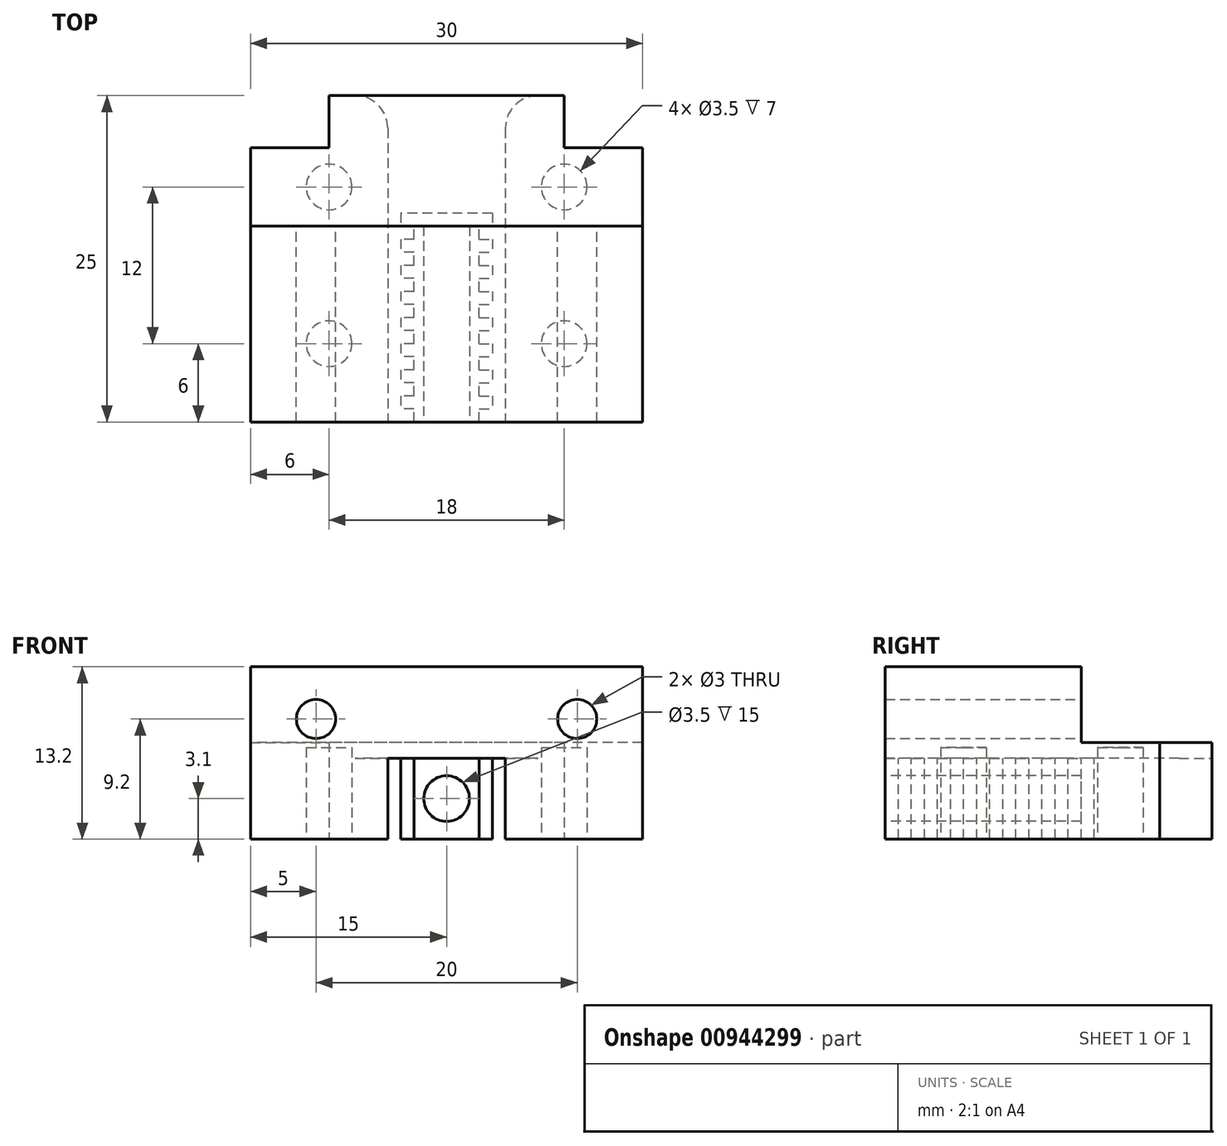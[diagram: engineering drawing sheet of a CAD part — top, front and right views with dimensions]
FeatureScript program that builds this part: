
annotation { "Feature Type Name" : "Feature", "Feature Type Description" : "" }
export const myFeature = defineFeature(function(context is Context, id is Id, definition is map)
    precondition{}
    {
        {
            var Q0;
            Q0=qCreatedBy(makeId("Front.planeOp"),FACE);
            var sketch = newSketch(context, id + "F0", { "sketchPlane" : qUnion([Q0])});
            skLineSegment(sketch, "E0.bottom", {"start": v(15, -3) * mm, "end": v(-15, -3) * mm});
            skLineSegment(sketch, "E0.top", {"start": v(15, 4) * mm, "end": v(-15, 4) * mm});
            skLineSegment(sketch, "E0.left", {"start": v(15, -3) * mm, "end": v(15, 4) * mm});
            skLineSegment(sketch, "E0.right", {"start": v(-15, -3) * mm, "end": v(-15, 4) * mm});
            skPoint(sketch, "E0.middle", {"position": v(0, 0) * mm});
            skCircle(sketch, "E1", {"center": v(-10, 0) * mm, "radius": 1.5 * mm});
            skCircle(sketch, "E2.MirrorC", {"center": v(10, 0) * mm, "radius": 1.5 * mm});
            skSolve(sketch);
        }
        {
            var Q0;
            Q0=makeQuery(id+"F0.imprint","IMPRINT",FACE,{"disambiguationData":[TD([[makeQuery(id+"F0.imprint","IMPRINT",EDGE,{"derivedFrom":sQuery(id+"F0.wireOp",EDGE,"E0.bottom")}),-1.0]])]});
            extrude(context, id + "F1", {"entities" : qUnion([Q0]), "depth" : 25 * mm, "offsetDistance" : 25 * mm});
        }
        {
            var Q0;
            Q0=makeQuery(id+"F1.opExtrude","SWEPT_FACE",FACE,{"disambiguationData":[OSD([sQuery(id+"F0.wireOp",EDGE,"E0.bottom")])]});
            var sketch = newSketch(context, id + "F2", { "sketchPlane" : qUnion([Q0])});
            skLineSegment(sketch, "E3", {"start": v(-2.5, 25) * mm, "end": v(-2.5, 24) * mm});
            skLineSegment(sketch, "E4.top", {"start": v(-3.5, 23) * mm, "end": v(-3.5, 24) * mm});
            skLineSegment(sketch, "E4.left", {"start": v(-2.5, 23) * mm, "end": v(-3.5, 23) * mm});
            skLineSegment(sketch, "E4.right", {"start": v(-2.5, 24) * mm, "end": v(-3.5, 24) * mm});
            skLineSegment(sketch, "E5.1.0.0", {"start": v(-2.5, 21) * mm, "end": v(-3.5, 21) * mm});
            skLineSegment(sketch, "E5.1.0.1", {"start": v(-3.5, 21) * mm, "end": v(-3.5, 22) * mm});
            skLineSegment(sketch, "E5.1.0.2", {"start": v(-2.5, 23) * mm, "end": v(-2.5, 22) * mm});
            skLineSegment(sketch, "E5.1.0.3", {"start": v(-2.5, 22) * mm, "end": v(-3.5, 22) * mm});
            skLineSegment(sketch, "E5.2.0.0", {"start": v(-2.5, 19) * mm, "end": v(-3.5, 19) * mm});
            skLineSegment(sketch, "E5.2.0.1", {"start": v(-3.5, 19) * mm, "end": v(-3.5, 20) * mm});
            skLineSegment(sketch, "E5.2.0.2", {"start": v(-2.5, 21) * mm, "end": v(-2.5, 20) * mm});
            skLineSegment(sketch, "E5.2.0.3", {"start": v(-2.5, 20) * mm, "end": v(-3.5, 20) * mm});
            skLineSegment(sketch, "E5.3.0.0", {"start": v(-2.5, 17) * mm, "end": v(-3.5, 17) * mm});
            skLineSegment(sketch, "E5.3.0.1", {"start": v(-3.5, 17) * mm, "end": v(-3.5, 18) * mm});
            skLineSegment(sketch, "E5.3.0.2", {"start": v(-2.5, 19) * mm, "end": v(-2.5, 18) * mm});
            skLineSegment(sketch, "E5.3.0.3", {"start": v(-2.5, 18) * mm, "end": v(-3.5, 18) * mm});
            skLineSegment(sketch, "E5.4.0.0", {"start": v(-2.5, 15) * mm, "end": v(-3.5, 15) * mm});
            skLineSegment(sketch, "E5.4.0.1", {"start": v(-3.5, 15) * mm, "end": v(-3.5, 16) * mm});
            skLineSegment(sketch, "E5.4.0.2", {"start": v(-2.5, 17) * mm, "end": v(-2.5, 16) * mm});
            skLineSegment(sketch, "E5.4.0.3", {"start": v(-2.5, 16) * mm, "end": v(-3.5, 16) * mm});
            skLineSegment(sketch, "E5.5.0.0", {"start": v(-2.5, 13) * mm, "end": v(-3.5, 13) * mm});
            skLineSegment(sketch, "E5.5.0.1", {"start": v(-3.5, 13) * mm, "end": v(-3.5, 14) * mm});
            skLineSegment(sketch, "E5.5.0.2", {"start": v(-2.5, 15) * mm, "end": v(-2.5, 14) * mm});
            skLineSegment(sketch, "E5.5.0.3", {"start": v(-2.5, 14) * mm, "end": v(-3.5, 14) * mm});
            skLineSegment(sketch, "E5.6.0.0", {"start": v(-2.5, 11) * mm, "end": v(-3.5, 11) * mm});
            skLineSegment(sketch, "E5.6.0.1", {"start": v(-3.5, 11) * mm, "end": v(-3.5, 12) * mm});
            skLineSegment(sketch, "E5.6.0.2", {"start": v(-2.5, 13) * mm, "end": v(-2.5, 12) * mm});
            skLineSegment(sketch, "E5.6.0.3", {"start": v(-2.5, 12) * mm, "end": v(-3.5, 12) * mm});
            skLineSegment(sketch, "E5.7.0.0", {"start": v(-2.5, 9) * mm, "end": v(-3.5, 9) * mm});
            skLineSegment(sketch, "E5.7.0.1", {"start": v(-3.5, 9) * mm, "end": v(-3.5, 10) * mm});
            skLineSegment(sketch, "E5.7.0.2", {"start": v(-2.5, 11) * mm, "end": v(-2.5, 10) * mm});
            skLineSegment(sketch, "E5.7.0.3", {"start": v(-2.5, 10) * mm, "end": v(-3.5, 10) * mm});
            skLineSegment(sketch, "E5.direction1", {"start": v(-2.5, 23) * mm, "end": v(-2.5, 21) * mm, "construction": true});
            skLineSegment(sketch, "E6", {"start": v(0, 0) * mm, "end": v(0, 25) * mm, "construction": true});
            skLineSegment(sketch, "E7.MirrorCS", {"start": v(2.5, 23) * mm, "end": v(2.5, 22) * mm});
            skLineSegment(sketch, "E8.MirrorCS", {"start": v(2.5, 25) * mm, "end": v(2.5, 24) * mm});
            skLineSegment(sketch, "E9.MirrorCS", {"start": v(2.5, 19) * mm, "end": v(3.5, 19) * mm});
            skLineSegment(sketch, "E10.MirrorCS", {"start": v(2.5, 16) * mm, "end": v(3.5, 16) * mm});
            skLineSegment(sketch, "E11.MirrorCS", {"start": v(2.5, 18) * mm, "end": v(3.5, 18) * mm});
            skLineSegment(sketch, "E12.MirrorCS", {"start": v(2.5, 22) * mm, "end": v(3.5, 22) * mm});
            skLineSegment(sketch, "E13.MirrorCS", {"start": v(2.5, 21) * mm, "end": v(3.5, 21) * mm});
            skLineSegment(sketch, "E14.MirrorCS", {"start": v(3.5, 9) * mm, "end": v(3.5, 10) * mm});
            skLineSegment(sketch, "E15.MirrorCS", {"start": v(2.5, 24) * mm, "end": v(3.5, 24) * mm});
            skLineSegment(sketch, "E16.MirrorCS", {"start": v(2.5, 9) * mm, "end": v(3.5, 9) * mm});
            skLineSegment(sketch, "E17.MirrorCS", {"start": v(2.5, 21) * mm, "end": v(2.5, 20) * mm});
            skLineSegment(sketch, "E18.MirrorCS", {"start": v(3.5, 11) * mm, "end": v(3.5, 12) * mm});
            skLineSegment(sketch, "E19.MirrorCS", {"start": v(2.5, 12) * mm, "end": v(3.5, 12) * mm});
            skLineSegment(sketch, "E20.MirrorCS", {"start": v(2.5, 17) * mm, "end": v(2.5, 16) * mm});
            skLineSegment(sketch, "E21.MirrorCS", {"start": v(2.5, 23) * mm, "end": v(2.5, 21) * mm, "construction": true});
            skLineSegment(sketch, "E22.MirrorCS", {"start": v(2.5, 15) * mm, "end": v(3.5, 15) * mm});
            skLineSegment(sketch, "E23.MirrorCS", {"start": v(3.5, 19) * mm, "end": v(3.5, 20) * mm});
            skLineSegment(sketch, "E24.MirrorCS", {"start": v(3.5, 15) * mm, "end": v(3.5, 16) * mm});
            skLineSegment(sketch, "E25.MirrorCS", {"start": v(2.5, 19) * mm, "end": v(2.5, 18) * mm});
            skLineSegment(sketch, "E26.MirrorCS", {"start": v(3.5, 21) * mm, "end": v(3.5, 22) * mm});
            skLineSegment(sketch, "E27.MirrorCS", {"start": v(2.5, 15) * mm, "end": v(2.5, 14) * mm});
            skLineSegment(sketch, "E28.MirrorCS", {"start": v(3.5, 23) * mm, "end": v(3.5, 24) * mm});
            skLineSegment(sketch, "E29.MirrorCS", {"start": v(2.5, 13) * mm, "end": v(2.5, 12) * mm});
            skLineSegment(sketch, "E30.MirrorCS", {"start": v(2.5, 20) * mm, "end": v(3.5, 20) * mm});
            skLineSegment(sketch, "E31.MirrorCS", {"start": v(2.5, 11) * mm, "end": v(2.5, 10) * mm});
            skLineSegment(sketch, "E32.MirrorCS", {"start": v(2.5, 14) * mm, "end": v(3.5, 14) * mm});
            skLineSegment(sketch, "E33.MirrorCS", {"start": v(3.5, 13) * mm, "end": v(3.5, 14) * mm});
            skLineSegment(sketch, "E34.MirrorCS", {"start": v(2.5, 23) * mm, "end": v(3.5, 23) * mm});
            skLineSegment(sketch, "E35.MirrorCS", {"start": v(2.5, 17) * mm, "end": v(3.5, 17) * mm});
            skLineSegment(sketch, "E36.MirrorCS", {"start": v(2.5, 13) * mm, "end": v(3.5, 13) * mm});
            skLineSegment(sketch, "E37.MirrorCS", {"start": v(3.5, 17) * mm, "end": v(3.5, 18) * mm});
            skLineSegment(sketch, "E38.MirrorCS", {"start": v(2.5, 11) * mm, "end": v(3.5, 11) * mm});
            skLineSegment(sketch, "E39.MirrorCS", {"start": v(2.5, 10) * mm, "end": v(3.5, 10) * mm});
            skLineSegment(sketch, "E40.MirrorCS", {"start": v(4.5, 2.5) * mm, "end": v(4.5, 25) * mm});
            skLineSegment(sketch, "E41", {"start": v(15, 25) * mm, "end": v(4.5, 25) * mm});
            skLineSegment(sketch, "E42", {"start": v(2.5, 9) * mm, "end": v(-2.5, 9) * mm});
            skArc(sketch, "E43", {"start": v(4.5, 2.5) * mm, "mid": v(5.23, 0.73) * mm, "end": v(7, 0) * mm});
            skPoint(sketch, "E43.third.point", {"position": v(4.69, 1.55) * mm});
            skLineSegment(sketch, "E44.MirrorCS", {"start": v(-15, 25) * mm, "end": v(-4.5, 25) * mm});
            skLineSegment(sketch, "E45.MirrorCS", {"start": v(-4.5, 2.5) * mm, "end": v(-4.5, 25) * mm});
            skArc(sketch, "E46.MirrorCS", {"start": v(-4.5, 2.5) * mm, "mid": v(-5.23, 0.73) * mm, "end": v(-7, 0) * mm});
            skPoint(sketch, "E47.orphan", {"position": v(15, 0) * mm});
            skLineSegment(sketch, "E48", {"start": v(7, 0) * mm, "end": v(15, 0) * mm});
            skLineSegment(sketch, "E49.MirrorCS", {"start": v(-7, 0) * mm, "end": v(-15, 0) * mm});
            skLineSegment(sketch, "E50", {"start": v(15, 0) * mm, "end": v(15, 25) * mm});
            skLineSegment(sketch, "E51.MirrorCS", {"start": v(-15, 0) * mm, "end": v(-15, 25) * mm});
            skSolve(sketch);
        }
        {
            var Q0;
            {var subQ1=sQuery(id+"F2.wireOp",EDGE,"E3");Q0=makeQuery(id+"F2.imprint","IMPRINT",FACE,{"disambiguationData":[TD([[makeQuery(id+"F2.imprint","IMPRINT",EDGE,{"derivedFrom":subQ1}),1.0]])]});}
            extrude(context, id + "F3", {"entities" : qUnion([Q0]), "depth" : 6.2 * mm, "offsetDistance" : 25 * mm});
        }
        {
            var Q0;
            Q0=qSketchRegion(id+"F2",true);
            extrude(context, id + "F4", {"entities" : qUnion([Q0]), "operationType" : NewBodyOperationType.ADD, "depth" : 6.2 * mm, "offsetDistance" : 25 * mm});
        }
        {
            var Q0;
            Q0=makeQuery(id+"F3.opExtrude","SWEPT_FACE",FACE,{"disambiguationData":[OSD([sQuery(id+"F0.wireOp",EDGE,"E0.bottom")])]});
            var sketch = newSketch(context, id + "F5", { "sketchPlane" : qUnion([Q0])});
            skLineSegment(sketch, "E52", {"start": v(0, -3) * mm, "end": v(0, -9.2) * mm, "construction": true});
            skLineSegment(sketch, "E53", {"start": v(0, -9.2) * mm, "end": v(-0.2, -9.17) * mm, "construction": true});
            skLineSegment(sketch, "E54", {"start": v(-2.5, -6.1) * mm, "end": v(2.5, -6.1) * mm, "construction": true});
            skCircle(sketch, "E55", {"center": v(0, -6.1) * mm, "radius": 1.75 * mm});
            skSolve(sketch);
        }
        {
            var Q0;
            Q0=makeQuery(id+"F5.imprint","IMPRINT",FACE,{"disambiguationData":[TD([[makeQuery(id+"F5.imprint","IMPRINT",EDGE,{"derivedFrom":sQuery(id+"F5.wireOp",EDGE,"E55")}),1.0]])]});
            extrude(context, id + "F6", {"entities" : qUnion([Q0]), "operationType" : NewBodyOperationType.REMOVE, "oppositeDirection" : true, "depth" : 15 * mm, "offsetDistance" : 25 * mm});
        }
        {
            var Q0;
            Q0=makeQuery(id+"F4.opExtrude","CAP_FACE",FACE,{"disambiguationData":[OSD([sQuery(id+"F2.wireOp",EDGE,"E40.MirrorCS"),sQuery(id+"F2.wireOp",EDGE,"E106.MirrorCS"),sQuery(id+"F2.wireOp",EDGE,"uDWrI3Gg-zkA3-hD0M-eEkA-WAwzIKrFUl89"),sQuery(id+"F2.wireOp",EDGE,"PeOV0Odv-COQw-PBpD-46EP-3vDGwS63vzDW"),sQuery(id+"F2.wireOp",EDGE,"E41")])],"isStart":false});
            var sketch = newSketch(context, id + "F7", { "sketchPlane" : qUnion([Q0])});
            skLineSegment(sketch, "E56", {"start": v(9, 3.36) * mm, "end": v(9, 25.43) * mm, "construction": true});
            skCircle(sketch, "E57", {"center": v(9, 7) * mm, "radius": 1.75 * mm});
            skCircle(sketch, "E58", {"center": v(9, 19) * mm, "radius": 1.75 * mm});
            skCircle(sketch, "E59.MirrorC", {"center": v(-9, 7) * mm, "radius": 1.75 * mm});
            skCircle(sketch, "E60.MirrorC", {"center": v(-9, 19) * mm, "radius": 1.75 * mm});
            skSolve(sketch);
        }
        {
            var Q0;
            Q0=qSketchRegion(id+"F7",true);
            extrude(context, id + "F8", {"entities" : qUnion([Q0]), "operationType" : NewBodyOperationType.REMOVE, "oppositeDirection" : true, "depth" : 7 * mm, "offsetDistance" : 25 * mm});
        }
        {
            var Q0;
            Q0=makeQuery(id+"F4.boolean.opBoolean","MERGE",FACE,{"derivedFrom":[makeQuery(id+"F1.opExtrude","CAP_FACE",FACE,{"disambiguationData":[OSD([sQuery(id+"F0.wireOp",EDGE,"E0.bottom"),sQuery(id+"F0.wireOp",EDGE,"E0.top"),sQuery(id+"F0.wireOp",EDGE,"E0.left"),sQuery(id+"F0.wireOp",EDGE,"E0.right"),sQuery(id+"F0.wireOp",EDGE,"E1"),sQuery(id+"F0.wireOp",EDGE,"E2.MirrorC")])],"isStart":true}),makeQuery(id+"F4.opExtrude","SWEPT_FACE",FACE,{"disambiguationData":[OSD([sQuery(id+"F2.wireOp",EDGE,"baEsnLOo-37dG-Q4tc-GQXZ-iAayZrFYDWQo")])]}),makeQuery(id+"F4.opExtrude","SWEPT_FACE",FACE,{"disambiguationData":[OSD([sQuery(id+"F2.wireOp",EDGE,"uDWrI3Gg-zkA3-hD0M-eEkA-WAwzIKrFUl89")])]})]});
            var sketch = newSketch(context, id + "F9", { "sketchPlane" : qUnion([Q0])});
            skLineSegment(sketch, "E61.bottom", {"start": v(-15, 4) * mm, "end": v(15, 4) * mm});
            skLineSegment(sketch, "E61.top", {"start": v(-15, -1.8) * mm, "end": v(15, -1.8) * mm});
            skLineSegment(sketch, "E61.left", {"start": v(-15, 4) * mm, "end": v(-15, -1.8) * mm});
            skLineSegment(sketch, "E61.right", {"start": v(15, 4) * mm, "end": v(15, -1.8) * mm});
            skSolve(sketch);
        }
        {
            var Q0;
            Q0=makeQuery(id+"F9.imprint","IMPRINT",FACE,{"disambiguationData":[TD([[makeQuery(id+"F9.imprint","IMPRINT",EDGE,{"derivedFrom":sQuery(id+"F9.wireOp",EDGE,"E61.bottom")}),-1.0]])]});
            extrude(context, id + "F10", {"entities" : qUnion([Q0]), "operationType" : NewBodyOperationType.REMOVE, "oppositeDirection" : true, "depth" : 10 * mm, "offsetDistance" : 25 * mm});
        }
        {
            var Q0;
            Q0=makeQuery(id+"F4.opExtrude","CAP_FACE",FACE,{"disambiguationData":[OSD([sQuery(id+"F2.wireOp",EDGE,"E44.MirrorCS"),sQuery(id+"F2.wireOp",EDGE,"E45.MirrorCS"),sQuery(id+"F2.wireOp",EDGE,"E46.MirrorCS"),sQuery(id+"F2.wireOp",EDGE,"E49.MirrorCS"),sQuery(id+"F2.wireOp",EDGE,"E51.MirrorCS")])],"isStart":false});
            var sketch = newSketch(context, id + "F11", { "sketchPlane" : qUnion([Q0])});
            skLineSegment(sketch, "E62.bottom", {"start": v(-15, 0) * mm, "end": v(-9, 0) * mm});
            skLineSegment(sketch, "E62.top", {"start": v(-15, 4) * mm, "end": v(-9, 4) * mm});
            skLineSegment(sketch, "E62.left", {"start": v(-15, 0) * mm, "end": v(-15, 4) * mm});
            skLineSegment(sketch, "E62.right", {"start": v(-9, 0) * mm, "end": v(-9, 4) * mm});
            skLineSegment(sketch, "E63.MirrorCS", {"start": v(9, 0) * mm, "end": v(9, 4) * mm});
            skLineSegment(sketch, "E64.MirrorCS", {"start": v(15, 4) * mm, "end": v(9, 4) * mm});
            skLineSegment(sketch, "E65.MirrorCS", {"start": v(15, 0) * mm, "end": v(15, 4) * mm});
            skLineSegment(sketch, "E66.MirrorCS", {"start": v(15, 0) * mm, "end": v(9, 0) * mm});
            skSolve(sketch);
        }
        {
            var Q0;
            Q0=makeQuery(id+"F11.imprint","IMPRINT",FACE,{"disambiguationData":[TD([[makeQuery(id+"F11.imprint","IMPRINT",EDGE,{"derivedFrom":sQuery(id+"F11.wireOp",EDGE,"E62.bottom")}),-1.0]])]});
            var Q1;
            Q1=makeQuery(id+"F11.imprint","IMPRINT",FACE,{"disambiguationData":[TD([[makeQuery(id+"F11.imprint","IMPRINT",EDGE,{"derivedFrom":sQuery(id+"F11.wireOp",EDGE,"E63.MirrorCS")}),-1.0]])]});
            extrude(context, id + "F12", {"entities" : qUnion([Q0, Q1]), "operationType" : NewBodyOperationType.REMOVE, "endBound" : BoundingType.THROUGH_ALL, "oppositeDirection" : true, "depth" : 25 * mm, "offsetDistance" : 25 * mm});
        }
    });
